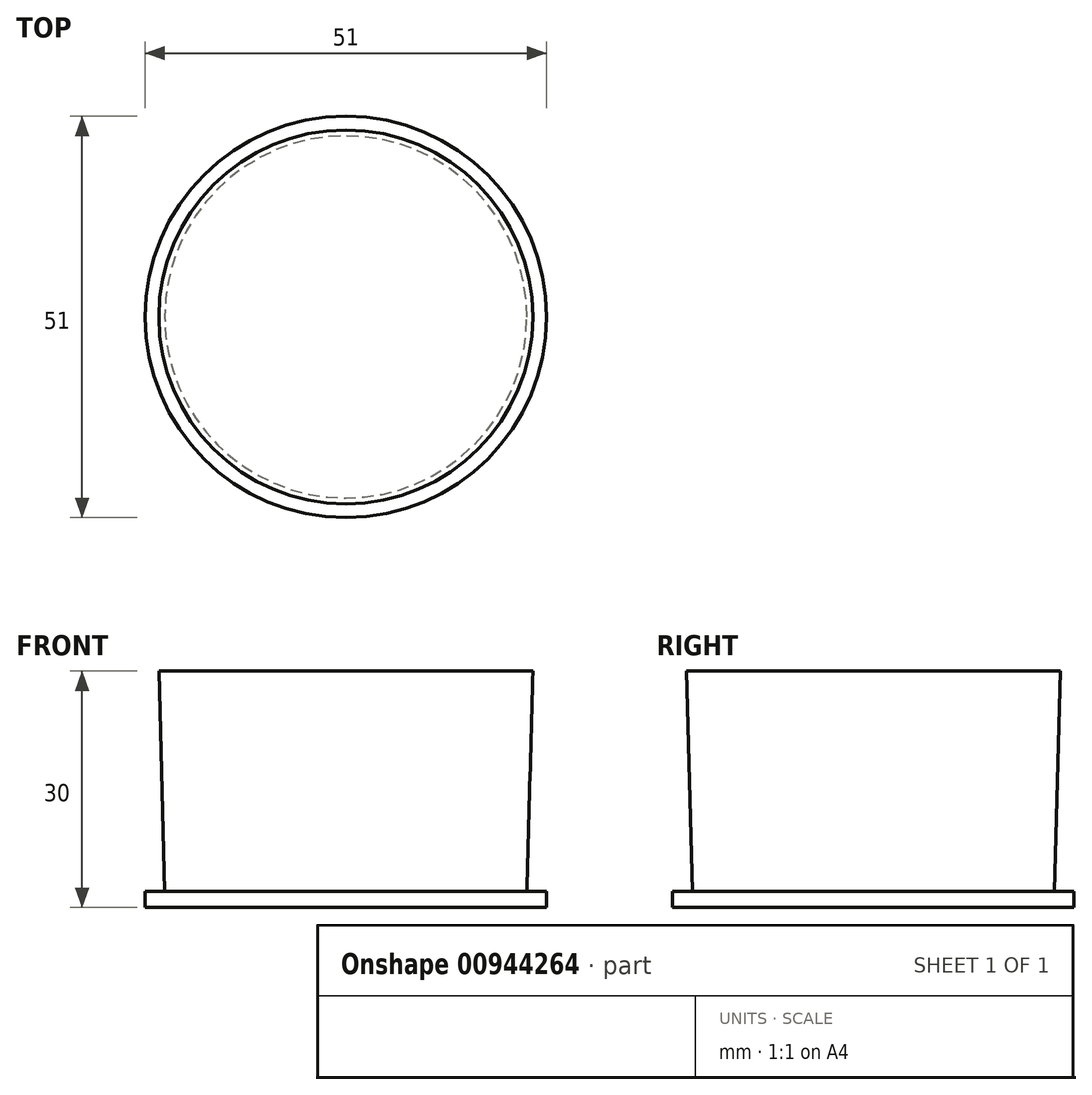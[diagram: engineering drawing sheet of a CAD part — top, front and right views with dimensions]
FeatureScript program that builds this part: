
annotation { "Feature Type Name" : "Feature", "Feature Type Description" : "" }
export const myFeature = defineFeature(function(context is Context, id is Id, definition is map)
    precondition{}
    {
        {
            var Q0;
            Q0=qCreatedBy(makeId("Front.planeOp"),FACE);
            var sketch = newSketch(context, id + "F0", { "sketchPlane" : qUnion([Q0])});
            skLineSegment(sketch, "E0", {"start": v(0, 0) * mm, "end": v(-25.5, 0) * mm});
            skLineSegment(sketch, "E1", {"start": v(-25.5, 0) * mm, "end": v(-25.5, 2) * mm});
            skLineSegment(sketch, "E2", {"start": v(-25.5, 2) * mm, "end": v(-23, 2) * mm});
            skLineSegment(sketch, "E3", {"start": v(-23, 2) * mm, "end": v(-23.75, 30) * mm});
            skLineSegment(sketch, "E4", {"start": v(-23.75, 30) * mm, "end": v(0, 30) * mm});
            skLineSegment(sketch, "E5", {"start": v(0, 30) * mm, "end": v(0, 0) * mm});
            skSolve(sketch);
        }
        {
            var Q0;
            Q0=makeQuery(id+"F0.imprint","IMPRINT",FACE,{"disambiguationData":[TD([[makeQuery(id+"F0.imprint","IMPRINT",EDGE,{"derivedFrom":sQuery(id+"F0.wireOp",EDGE,"E0")}),-1.0]])]});
            var Q1;
            Q1=sQuery(id+"F0.wireOp",EDGE,"E5");
            revolve(context, id + "F1", {"surfaceOperationType" : NewSurfaceOperationType.NEW, "entities" : qUnion([Q0]), "axis" : qUnion([Q1]), "revolveType" : RevolveType.FULL});
        }
    });
